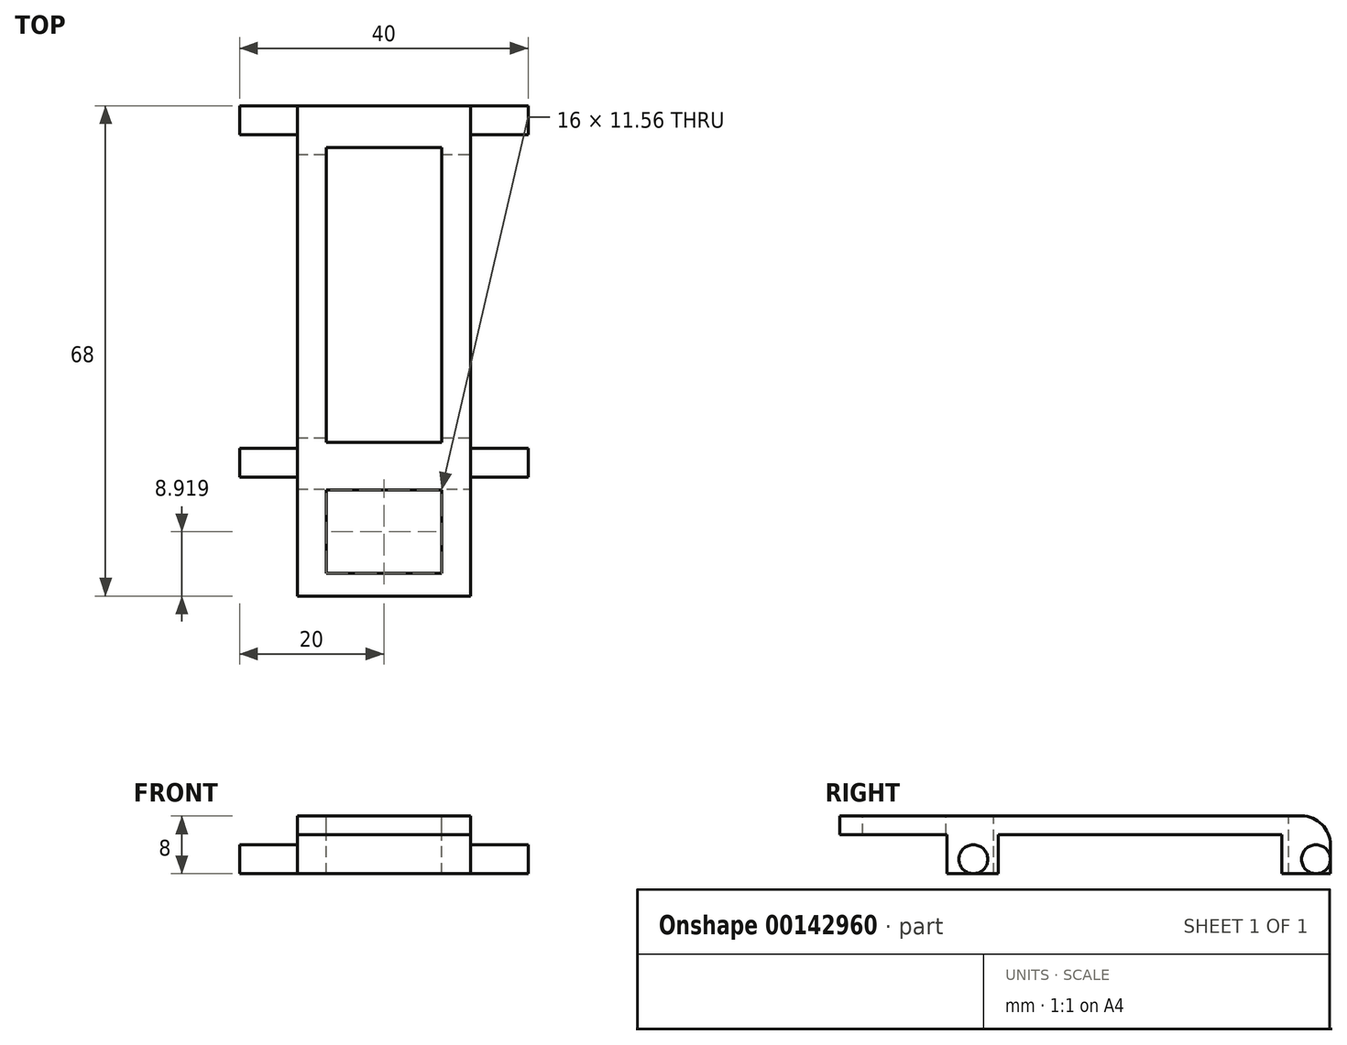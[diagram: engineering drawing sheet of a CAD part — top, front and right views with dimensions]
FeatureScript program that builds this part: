
annotation { "Feature Type Name" : "Feature", "Feature Type Description" : "" }
export const myFeature = defineFeature(function(context is Context, id is Id, definition is map)
    precondition{}
    {
        {
            var Q0;
            Q0=qCreatedBy(makeId("Top.planeOp"),FACE);
            var sketch = newSketch(context, id + "F0", { "sketchPlane" : qUnion([Q0])});
            skLineSegment(sketch, "E0.bottom", {"start": v(12, 34) * mm, "end": v(-12, 34) * mm});
            skLineSegment(sketch, "E0.top", {"start": v(12, -34) * mm, "end": v(-12, -34) * mm});
            skLineSegment(sketch, "E0.left", {"start": v(12, 34) * mm, "end": v(12, -34) * mm});
            skLineSegment(sketch, "E0.right", {"start": v(-12, 34) * mm, "end": v(-12, -34) * mm});
            skPoint(sketch, "E0.middle", {"position": v(0, 0) * mm});
            skSolve(sketch);
        }
        {
            var Q0;
            Q0 = qSketchRegion(id + "F0", true);
            extrude(context, id + "F1", {"entities" : qUnion([Q0]), "depth" : 8 * mm});
        }
        {
            var Q0;
            Q0=qCreatedBy(makeId("Right.planeOp"),FACE);
            var sketch = newSketch(context, id + "F2", { "sketchPlane" : qUnion([Q0])});
            skCircle(sketch, "E1", {"center": v(32, 2) * mm, "radius": 2 * mm});
            skCircle(sketch, "E2", {"center": v(-15.5, 2) * mm, "radius": 2 * mm});
            skSolve(sketch);
        }
        {
            var Q0;
            Q0 = qSketchRegion(id + "F2", true);
            extrude(context, id + "F3", {"entities" : qUnion([Q0]), "operationType" : NewBodyOperationType.ADD, "depth" : 40 * mm, "symmetric" : true});
        }
        {
            var Q0;
            {var subQ0=sQuery(id+"F0.wireOp",EDGE,"E0.top");var subQ1=sQuery(id+"F0.wireOp",EDGE,"E0.right");var subQ2=sQuery(id+"F0.wireOp",EDGE,"E0.left");var subQ3=sQuery(id+"F0.wireOp",EDGE,"E0.bottom");var subQ4=makeQuery(id+"F1.opExtrude","SWEPT_FACE",FACE,{"disambiguationData":[OSD([subQ2])]});Q0=makeQuery(id+"F3.boolean.opBoolean","SPLIT",FACE,{"disambiguationData":[TD([makeQuery(id+"F1.opExtrude","SWEPT_FACE",FACE,{"disambiguationData":[OSD([subQ3])]}),makeQuery(id+"F1.opExtrude","CAP_FACE",FACE,{"disambiguationData":[OSD([subQ3,subQ0,subQ2,subQ1])],"isStart":true}),makeQuery(id+"F1.opExtrude","CAP_FACE",FACE,{"disambiguationData":[OSD([subQ3,subQ0,subQ2,subQ1])],"isStart":false}),makeQuery(id+"F1.opExtrude","SWEPT_FACE",FACE,{"disambiguationData":[OSD([subQ0])]}),subQ4,makeQuery(id+"F3.opExtrude","SWEPT_FACE",FACE,{"disambiguationData":[OSD([sQuery(id+"F2.wireOp",EDGE,"E1")])]}),makeQuery(id+"F3.opExtrude","SWEPT_FACE",FACE,{"disambiguationData":[OSD([sQuery(id+"F2.wireOp",EDGE,"E2")])]})])],"derivedFrom":subQ4});}
            var sketch = newSketch(context, id + "F4", { "sketchPlane" : qUnion([Q0])});
            skLineSegment(sketch, "E3.0", {"start": v(34, 4) * mm, "end": v(34, 2) * mm});
            skLineSegment(sketch, "E4.0", {"start": v(30, 8) * mm, "end": v(-34, 8) * mm});
            skPoint(sketch, "E5.visualSharp", {"position": v(34, 8) * mm});
            skArc(sketch, "E5.filletArc", {"start": v(34, 4) * mm, "mid": v(32.83, 6.83) * mm, "end": v(30, 8) * mm});
            skLineSegment(sketch, "E6", {"start": v(30, 8) * mm, "end": v(34, 8) * mm});
            skLineSegment(sketch, "E7", {"start": v(34, 8) * mm, "end": v(34, 4) * mm});
            skLineSegment(sketch, "E8", {"start": v(-12.07, 0) * mm, "end": v(27.25, 0) * mm});
            skLineSegment(sketch, "E9", {"start": v(-34, 5.43) * mm, "end": v(-34, 0) * mm});
            skLineSegment(sketch, "E10", {"start": v(-34, 0) * mm, "end": v(-19.17, 0) * mm});
            skLineSegment(sketch, "E11.bottom", {"start": v(-19.17, 0) * mm, "end": v(-34, 0) * mm});
            skLineSegment(sketch, "E11.top", {"start": v(-19.17, 5.43) * mm, "end": v(-34, 5.43) * mm});
            skLineSegment(sketch, "E11.left", {"start": v(-19.17, 0) * mm, "end": v(-19.17, 5.43) * mm});
            skLineSegment(sketch, "E11.right", {"start": v(-34, 0) * mm, "end": v(-34, 5.43) * mm});
            skLineSegment(sketch, "E12.top", {"start": v(-12.07, 5.43) * mm, "end": v(27.25, 5.43) * mm});
            skLineSegment(sketch, "E12.left", {"start": v(-12.07, 0) * mm, "end": v(-12.07, 5.43) * mm});
            skLineSegment(sketch, "E12.right", {"start": v(27.25, 0) * mm, "end": v(27.25, 5.43) * mm});
            skSolve(sketch);
        }
        {
            var Q0;
            Q0 = qSketchRegion(id + "F4", true);
            extrude(context, id + "F5", {"entities" : qUnion([Q0]), "operationType" : NewBodyOperationType.REMOVE, "oppositeDirection" : true, "depth" : 25 * mm});
        }
        {
            var Q0;
            Q0=makeQuery(id+"F1.opExtrude","CAP_FACE",FACE,{"disambiguationData":[OSD([sQuery(id+"F0.wireOp",EDGE,"E0.bottom"),sQuery(id+"F0.wireOp",EDGE,"E0.top"),sQuery(id+"F0.wireOp",EDGE,"E0.left"),sQuery(id+"F0.wireOp",EDGE,"E0.right")])],"isStart":false});
            var sketch = newSketch(context, id + "F6", { "sketchPlane" : qUnion([Q0])});
            skLineSegment(sketch, "E13.bottom", {"start": v(-8, 28.23) * mm, "end": v(8, 28.23) * mm});
            skLineSegment(sketch, "E13.top", {"start": v(-8, -12.68) * mm, "end": v(8, -12.68) * mm});
            skLineSegment(sketch, "E13.left", {"start": v(-8, 28.23) * mm, "end": v(-8, -12.68) * mm});
            skLineSegment(sketch, "E13.right", {"start": v(8, 28.23) * mm, "end": v(8, -12.68) * mm});
            skLineSegment(sketch, "E14.bottom", {"start": v(-8, -19.3) * mm, "end": v(8, -19.3) * mm});
            skLineSegment(sketch, "E14.top", {"start": v(-8, -30.86) * mm, "end": v(8, -30.86) * mm});
            skLineSegment(sketch, "E14.left", {"start": v(-8, -19.3) * mm, "end": v(-8, -30.86) * mm});
            skLineSegment(sketch, "E14.right", {"start": v(8, -19.3) * mm, "end": v(8, -30.86) * mm});
            skSolve(sketch);
        }
        {
            var Q0;
            Q0 = qSketchRegion(id + "F6", true);
            extrude(context, id + "F7", {"entities" : qUnion([Q0]), "operationType" : NewBodyOperationType.REMOVE, "oppositeDirection" : true, "depth" : 25 * mm});
        }
    });
